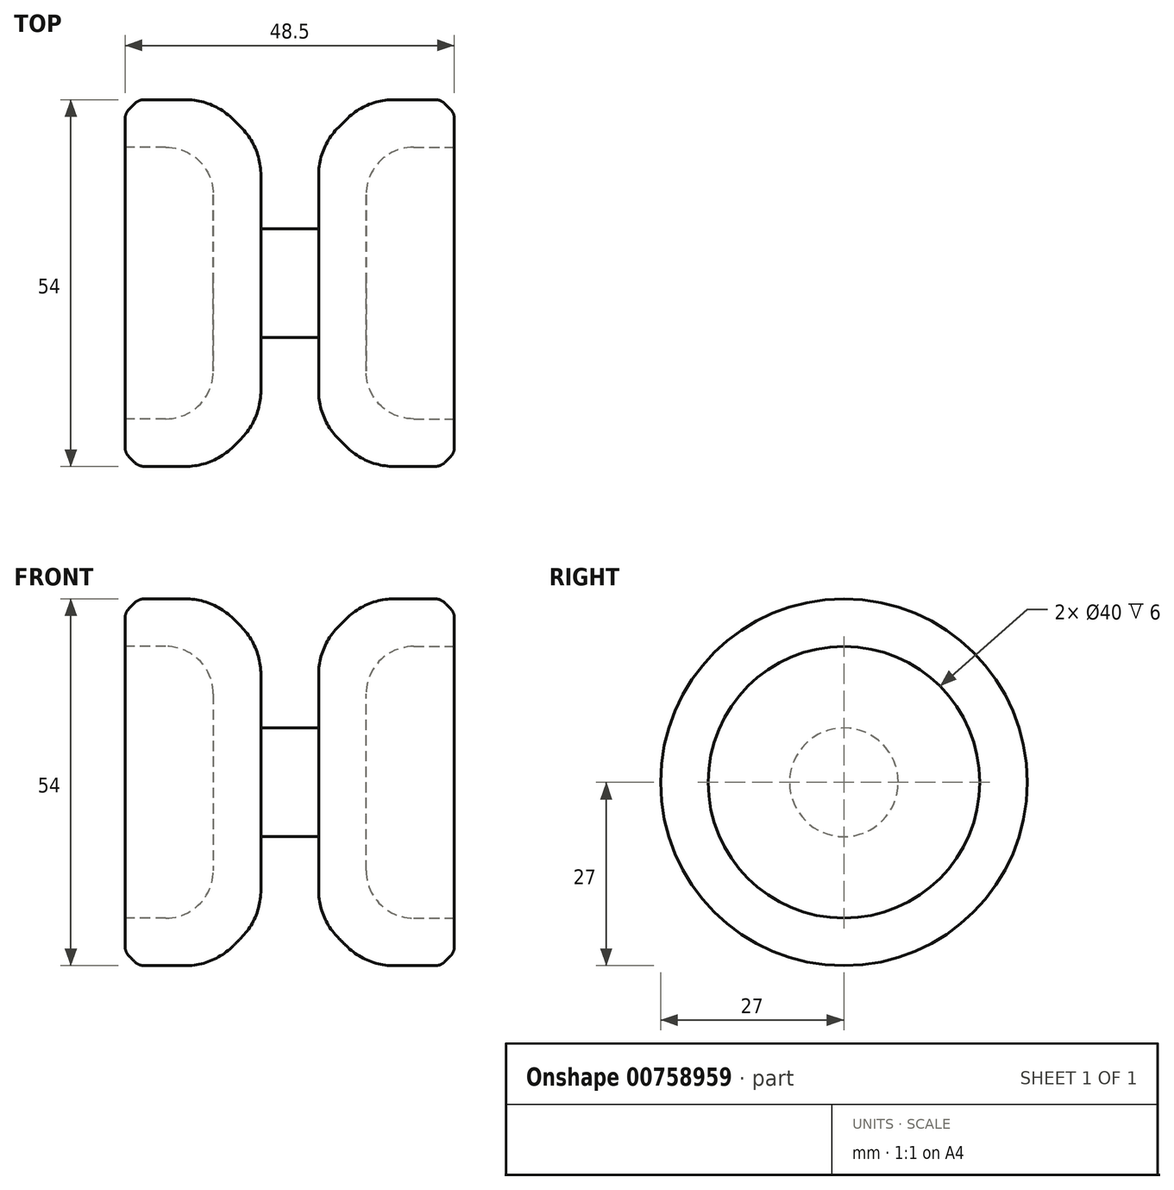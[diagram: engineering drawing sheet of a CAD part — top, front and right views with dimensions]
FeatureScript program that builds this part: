
annotation { "Feature Type Name" : "Feature", "Feature Type Description" : "" }
export const myFeature = defineFeature(function(context is Context, id is Id, definition is map)
    precondition{}
    {
        {
            var Q0;
            Q0=qCreatedBy(makeId("Top.planeOp"),FACE);
            var sketch = newSketch(context, id + "F0", { "sketchPlane" : qUnion([Q0])});
            skLineSegment(sketch, "E0", {"start": v(-4.25, 8) * mm, "end": v(0, 8) * mm});
            skLineSegment(sketch, "E1", {"start": v(-24.25, 27) * mm, "end": v(-4.25, 27) * mm});
            skLineSegment(sketch, "E2", {"start": v(-4.25, 27) * mm, "end": v(-4.25, 8) * mm});
            skLineSegment(sketch, "E3.MirrorCS", {"start": v(24.25, 27) * mm, "end": v(4.25, 27) * mm});
            skLineSegment(sketch, "E4.MirrorCS", {"start": v(4.25, 27) * mm, "end": v(4.25, 8) * mm});
            skLineSegment(sketch, "E5.MirrorCS", {"start": v(4.25, 8) * mm, "end": v(0, 8) * mm});
            skLineSegment(sketch, "E6", {"start": v(-24.25, 0) * mm, "end": v(24.25, 0) * mm});
            skLineSegment(sketch, "E7", {"start": v(-24.25, 27) * mm, "end": v(-24.25, 0) * mm});
            skLineSegment(sketch, "E8", {"start": v(24.25, 27) * mm, "end": v(24.25, 0) * mm});
            skSolve(sketch);
        }
        {
            var Q0;
            Q0 = qSketchRegion(id + "F0", true);
            var Q1;
            Q1=sQuery(id+"F0.wireOp",EDGE,"E6");
            revolve(context, id + "F1", {"surfaceOperationType" : NewSurfaceOperationType.NEW, "entities" : qUnion([Q0]), "axis" : qUnion([Q1]), "revolveType" : RevolveType.FULL});
        }
        {
            var Q0;
            Q0=makeQuery(id+"F1.opRevolve","SWEPT_EDGE",EDGE,{"disambiguationData":[OSD([sQuery(id+"F0.wireOp",EDGE,"E1"),sQuery(id+"F0.wireOp",EDGE,"E2")])]});
            var Q1;
            Q1=makeQuery(id+"F1.opRevolve","SWEPT_EDGE",EDGE,{"disambiguationData":[OSD([sQuery(id+"F0.wireOp",EDGE,"E3.MirrorCS"),sQuery(id+"F0.wireOp",EDGE,"E4.MirrorCS")])]});
            chamfer(context, id + "F2", {"entities" : qUnion([Q0, Q1]), "width" : 7 * mm, "tangentPropagation" : true});
        }
        {
            var Q0;
            {var subQ0=sQuery(id+"F0.wireOp",EDGE,"E2");Q0=makeQuery(id+"F2.opChamfer","BLEND_EDGE",EDGE,{"blendedFrom":[makeQuery(id+"F1.opRevolve","SWEPT_EDGE",EDGE,{"disambiguationData":[OSD([sQuery(id+"F0.wireOp",EDGE,"E1"),subQ0])]}),makeQuery(id+"F1.opRevolve","SWEPT_FACE",FACE,{"disambiguationData":[OSD([subQ0])]})],"blendedInto":[makeQuery(id+"F1.opRevolve","SWEPT_FACE",FACE,{"disambiguationData":[OSD([subQ0])]})]});}
            var Q1;
            {var subQ0=sQuery(id+"F0.wireOp",EDGE,"E1");Q1=makeQuery(id+"F2.opChamfer","BLEND_EDGE",EDGE,{"blendedFrom":[makeQuery(id+"F1.opRevolve","SWEPT_EDGE",EDGE,{"disambiguationData":[OSD([subQ0,sQuery(id+"F0.wireOp",EDGE,"E2")])]}),makeQuery(id+"F1.opRevolve","SWEPT_FACE",FACE,{"disambiguationData":[OSD([subQ0])]})],"blendedInto":[makeQuery(id+"F1.opRevolve","SWEPT_FACE",FACE,{"disambiguationData":[OSD([subQ0])]})]});}
            var Q2;
            {var subQ0=sQuery(id+"F0.wireOp",EDGE,"E4.MirrorCS");Q2=makeQuery(id+"F2.opChamfer","BLEND_EDGE",EDGE,{"blendedFrom":[makeQuery(id+"F1.opRevolve","SWEPT_EDGE",EDGE,{"disambiguationData":[OSD([sQuery(id+"F0.wireOp",EDGE,"E3.MirrorCS"),subQ0])]}),makeQuery(id+"F1.opRevolve","SWEPT_FACE",FACE,{"disambiguationData":[OSD([subQ0])]})],"blendedInto":[makeQuery(id+"F1.opRevolve","SWEPT_FACE",FACE,{"disambiguationData":[OSD([subQ0])]})]});}
            var Q3;
            {var subQ0=sQuery(id+"F0.wireOp",EDGE,"E3.MirrorCS");Q3=makeQuery(id+"F2.opChamfer","BLEND_EDGE",EDGE,{"blendedFrom":[makeQuery(id+"F1.opRevolve","SWEPT_EDGE",EDGE,{"disambiguationData":[OSD([subQ0,sQuery(id+"F0.wireOp",EDGE,"E4.MirrorCS")])]}),makeQuery(id+"F1.opRevolve","SWEPT_FACE",FACE,{"disambiguationData":[OSD([subQ0])]})],"blendedInto":[makeQuery(id+"F1.opRevolve","SWEPT_FACE",FACE,{"disambiguationData":[OSD([subQ0])]})]});}
            fillet(context, id + "F3", {"entities" : qUnion([Q0, Q1, Q2, Q3]), "radius" : 10 * mm, "tangentPropagation" : true, "allowEdgeOverflow" : false});
        }
        {
            var Q0;
            Q0=makeQuery(id+"F1.opRevolve","SWEPT_EDGE",EDGE,{"disambiguationData":[OSD([sQuery(id+"F0.wireOp",EDGE,"E1"),sQuery(id+"F0.wireOp",EDGE,"E7")])]});
            var Q1;
            Q1=makeQuery(id+"F1.opRevolve","SWEPT_EDGE",EDGE,{"disambiguationData":[OSD([sQuery(id+"F0.wireOp",EDGE,"E3.MirrorCS"),sQuery(id+"F0.wireOp",EDGE,"E8")])]});
            chamfer(context, id + "F4", {"entities" : qUnion([Q0, Q1]), "width" : 2 * mm, "tangentPropagation" : true});
        }
        {
            var Q0;
            {var subQ0=sQuery(id+"F0.wireOp",EDGE,"E1");Q0=makeQuery(id+"F4.opChamfer","BLEND_EDGE",EDGE,{"blendedFrom":[makeQuery(id+"F1.opRevolve","SWEPT_EDGE",EDGE,{"disambiguationData":[OSD([subQ0,sQuery(id+"F0.wireOp",EDGE,"E7")])]}),makeQuery(id+"F1.opRevolve","SWEPT_FACE",FACE,{"disambiguationData":[OSD([subQ0])]})],"blendedInto":[makeQuery(id+"F1.opRevolve","SWEPT_FACE",FACE,{"disambiguationData":[OSD([subQ0])]})]});}
            var Q1;
            {var subQ0=sQuery(id+"F0.wireOp",EDGE,"E3.MirrorCS");Q1=makeQuery(id+"F4.opChamfer","BLEND_EDGE",EDGE,{"blendedFrom":[makeQuery(id+"F1.opRevolve","SWEPT_EDGE",EDGE,{"disambiguationData":[OSD([subQ0,sQuery(id+"F0.wireOp",EDGE,"E8")])]}),makeQuery(id+"F1.opRevolve","SWEPT_FACE",FACE,{"disambiguationData":[OSD([subQ0])]})],"blendedInto":[makeQuery(id+"F1.opRevolve","SWEPT_FACE",FACE,{"disambiguationData":[OSD([subQ0])]})]});}
            var Q2;
            {var subQ0=sQuery(id+"F0.wireOp",EDGE,"E7");Q2=makeQuery(id+"F4.opChamfer","BLEND_EDGE",EDGE,{"blendedFrom":[makeQuery(id+"F1.opRevolve","SWEPT_EDGE",EDGE,{"disambiguationData":[OSD([sQuery(id+"F0.wireOp",EDGE,"E1"),subQ0])]}),makeQuery(id+"F1.opRevolve","SWEPT_FACE",FACE,{"disambiguationData":[OSD([subQ0])]})],"blendedInto":[makeQuery(id+"F1.opRevolve","SWEPT_FACE",FACE,{"disambiguationData":[OSD([subQ0])]})]});}
            var Q3;
            {var subQ0=sQuery(id+"F0.wireOp",EDGE,"E8");Q3=makeQuery(id+"F4.opChamfer","BLEND_EDGE",EDGE,{"blendedFrom":[makeQuery(id+"F1.opRevolve","SWEPT_EDGE",EDGE,{"disambiguationData":[OSD([sQuery(id+"F0.wireOp",EDGE,"E3.MirrorCS"),subQ0])]}),makeQuery(id+"F1.opRevolve","SWEPT_FACE",FACE,{"disambiguationData":[OSD([subQ0])]})],"blendedInto":[makeQuery(id+"F1.opRevolve","SWEPT_FACE",FACE,{"disambiguationData":[OSD([subQ0])]})]});}
            fillet(context, id + "F5", {"entities" : qUnion([Q0, Q1, Q2, Q3]), "radius" : 2 * mm, "tangentPropagation" : true, "allowEdgeOverflow" : false});
        }
        {
            var Q0;
            Q0=makeQuery(id+"F1.opRevolve","SWEPT_FACE",FACE,{"disambiguationData":[OSD([sQuery(id+"F0.wireOp",EDGE,"E8")])]});
            var sketch = newSketch(context, id + "F6", { "sketchPlane" : qUnion([Q0])});
            skCircle(sketch, "E9", {"center": v(0, 0) * mm, "radius": 20 * mm});
            skSolve(sketch);
        }
        {
            var Q0;
            Q0 = qSketchRegion(id + "F6", true);
            extrude(context, id + "F7", {"entities" : qUnion([Q0]), "operationType" : NewBodyOperationType.REMOVE, "oppositeDirection" : true, "depth" : 13 * mm, "offsetDistance" : 25 * mm});
        }
        {
            var Q0;
            Q0=makeQuery(id+"F1.opRevolve","SWEPT_FACE",FACE,{"disambiguationData":[OSD([sQuery(id+"F0.wireOp",EDGE,"E7")])]});
            var sketch = newSketch(context, id + "F8", { "sketchPlane" : qUnion([Q0])});
            skCircle(sketch, "E10", {"center": v(0, 0) * mm, "radius": 20 * mm});
            skSolve(sketch);
        }
        {
            var Q0;
            Q0 = qSketchRegion(id + "F8", true);
            extrude(context, id + "F9", {"entities" : qUnion([Q0]), "operationType" : NewBodyOperationType.REMOVE, "oppositeDirection" : true, "depth" : 13 * mm, "offsetDistance" : 25 * mm});
        }
        {
            var Q0;
            Q0=makeQuery(id+"F7.boolean.opBoolean","COPY",EDGE,{"derivedFrom":makeQuery(id+"F7.opExtrude","CAP_EDGE",EDGE,{"disambiguationData":[OSD([sQuery(id+"F6.wireOp",EDGE,"E9")])],"isStart":false})});
            var Q1;
            Q1=makeQuery(id+"F9.boolean.opBoolean","COPY",EDGE,{"derivedFrom":makeQuery(id+"F9.opExtrude","CAP_EDGE",EDGE,{"disambiguationData":[OSD([sQuery(id+"F8.wireOp",EDGE,"E10")])],"isStart":false})});
            fillet(context, id + "F10", {"entities" : qUnion([Q0, Q1]), "radius" : 7 * mm, "tangentPropagation" : true, "allowEdgeOverflow" : false});
        }
    });
